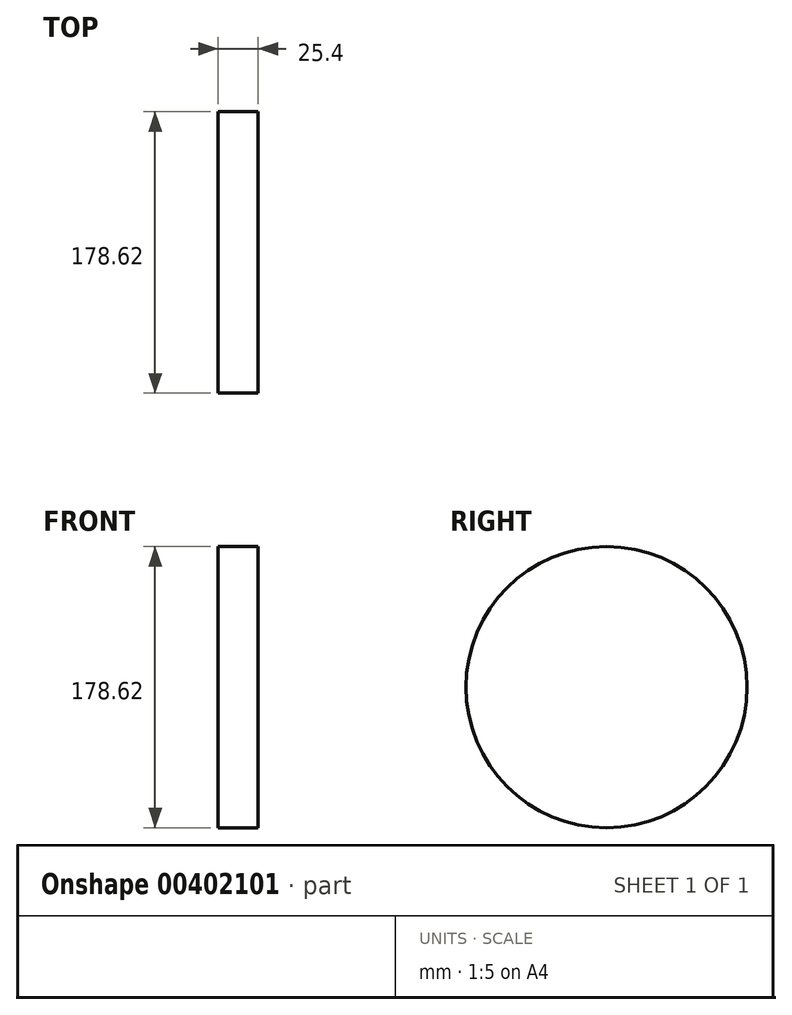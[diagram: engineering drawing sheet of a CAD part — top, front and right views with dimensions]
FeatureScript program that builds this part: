
annotation { "Feature Type Name" : "Feature", "Feature Type Description" : "" }
export const myFeature = defineFeature(function(context is Context, id is Id, definition is map)
    precondition{}
    {
        {
            var Q0;
            Q0=qCreatedBy(makeId("Right.planeOp"),FACE);
            var sketch = newSketch(context, id + "F0", { "sketchPlane" : qUnion([Q0])});
            skCircle(sketch, "E0", {"center": v(0, 0) * mm, "radius": 89.3 * mm});
            skSolve(sketch);
        }
        {
            var Q0;
            Q0=makeQuery(id+"F0.imprint","IMPRINT",FACE,{"disambiguationData":[TD([[makeQuery(id+"F0.imprint","IMPRINT",EDGE,{"derivedFrom":sQuery(id+"F0.wireOp",EDGE,"E0")}),1.0]])]});
            extrude(context, id + "F1", {"entities" : qUnion([Q0]), "depth" : 25.4 * mm});
        }
    });
